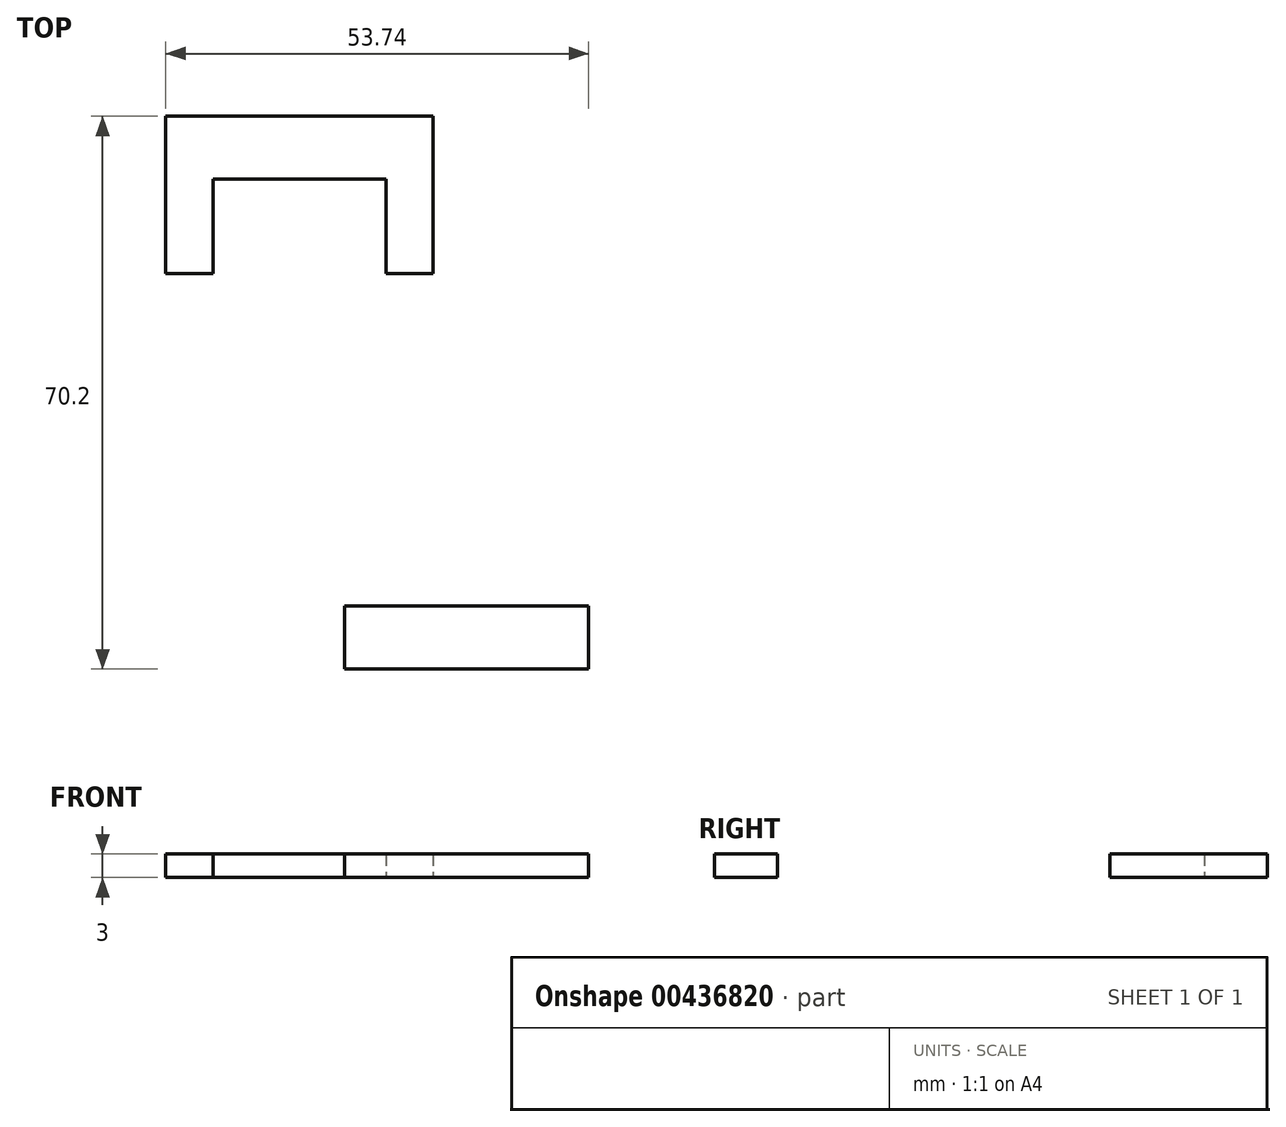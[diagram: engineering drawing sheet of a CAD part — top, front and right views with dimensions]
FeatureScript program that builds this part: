
annotation { "Feature Type Name" : "Feature", "Feature Type Description" : "" }
export const myFeature = defineFeature(function(context is Context, id is Id, definition is map)
    precondition{}
    {
        {
            var Q0;
            Q0=qCreatedBy(makeId("Top.planeOp"),FACE);
            var sketch = newSketch(context, id + "F0", { "sketchPlane" : qUnion([Q0])});
            skLineSegment(sketch, "E0", {"start": v(-71.25, 20) * mm, "end": v(-37.25, 20) * mm});
            skLineSegment(sketch, "E1", {"start": v(-37.25, 20) * mm, "end": v(-37.25, 0) * mm});
            skLineSegment(sketch, "E2", {"start": v(-37.25, 0) * mm, "end": v(-43.25, 0) * mm});
            skLineSegment(sketch, "E3", {"start": v(-43.25, 0) * mm, "end": v(-43.25, 12) * mm});
            skLineSegment(sketch, "E4", {"start": v(-43.25, 12) * mm, "end": v(-65.25, 12) * mm});
            skLineSegment(sketch, "E5", {"start": v(-65.25, 12) * mm, "end": v(-65.25, 0) * mm});
            skLineSegment(sketch, "E6", {"start": v(-65.25, 0) * mm, "end": v(-70.25, 0) * mm});
            skLineSegment(sketch, "E7", {"start": v(-71.25, 20) * mm, "end": v(-71.25, 0) * mm});
            skLineSegment(sketch, "E8", {"start": v(-65.25, 0) * mm, "end": v(-71.25, 0) * mm});
            skLineSegment(sketch, "E9", {"start": v(-48.51, -50.2) * mm, "end": v(-17.51, -50.2) * mm});
            skLineSegment(sketch, "E10", {"start": v(-17.51, -50.2) * mm, "end": v(-17.51, -42.2) * mm});
            skLineSegment(sketch, "E11", {"start": v(-17.51, -42.2) * mm, "end": v(-48.51, -42.2) * mm});
            skLineSegment(sketch, "E12", {"start": v(-48.51, -42.2) * mm, "end": v(-48.51, -50.2) * mm});
            skSolve(sketch);
        }
        {
            var Q0;
            Q0 = qSketchRegion(id + "F0", true);
            extrude(context, id + "F1", {"entities" : qUnion([Q0]), "depth" : 3 * mm});
        }
    });
